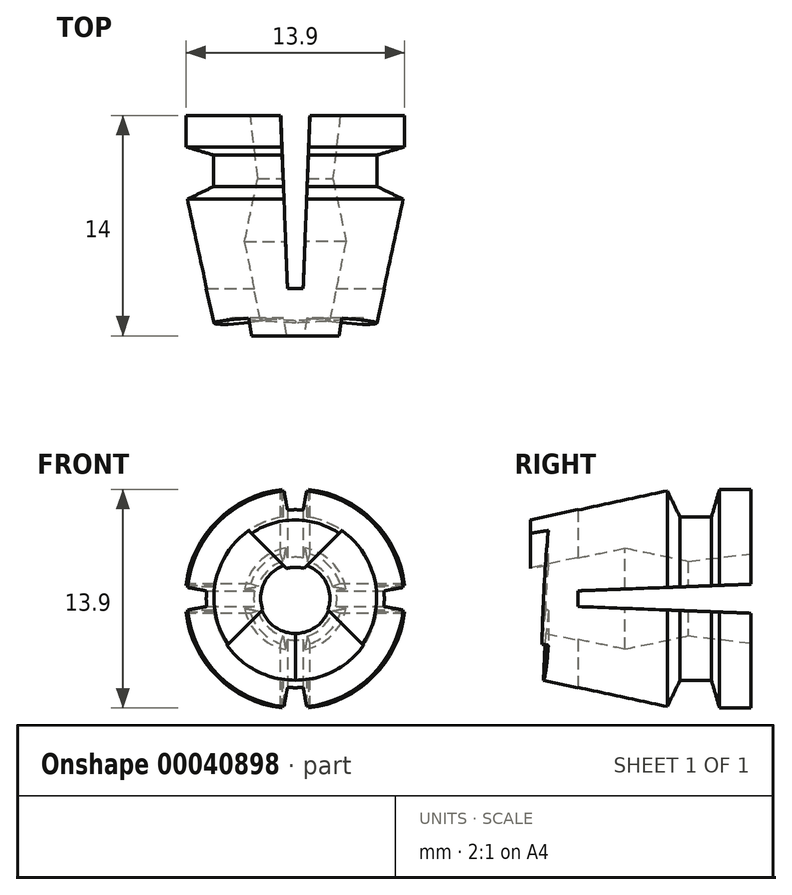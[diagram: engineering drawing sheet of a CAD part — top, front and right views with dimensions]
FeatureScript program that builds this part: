
annotation { "Feature Type Name" : "Feature", "Feature Type Description" : "" }
export const myFeature = defineFeature(function(context is Context, id is Id, definition is map)
    precondition{}
    {
        {
            var Q0;
            Q0=qCreatedBy(makeId("Top.planeOp"),FACE);
            var sketch = newSketch(context, id + "F0", { "sketchPlane" : qUnion([Q0])});
            skLineSegment(sketch, "E0", {"start": v(3, 14) * mm, "end": v(7, 14) * mm});
            skLineSegment(sketch, "E1", {"start": v(7, 14) * mm, "end": v(7, 12) * mm});
            skLineSegment(sketch, "E2", {"start": v(6.89, 8.67) * mm, "end": v(5, 0) * mm});
            skLineSegment(sketch, "E3", {"start": v(5, 0) * mm, "end": v(2, 0) * mm});
            skLineSegment(sketch, "E4", {"start": v(2, 0) * mm, "end": v(3.28, 6) * mm});
            skLineSegment(sketch, "E5", {"start": v(3.28, 6) * mm, "end": v(3.28, 6) * mm});
            skLineSegment(sketch, "E6", {"start": v(3.28, 6) * mm, "end": v(2.5, 10) * mm});
            skLineSegment(sketch, "E7", {"start": v(2.5, 10) * mm, "end": v(2.38, 10) * mm});
            skLineSegment(sketch, "E8", {"start": v(2.5, 10) * mm, "end": v(3, 14) * mm});
            skLineSegment(sketch, "E9", {"start": v(0, 20.25) * mm, "end": v(0, -12.85) * mm, "construction": true});
            skLineSegment(sketch, "E10", {"start": v(7, 12) * mm, "end": v(5.25, 11.48) * mm});
            skLineSegment(sketch, "E11", {"start": v(5.25, 11.48) * mm, "end": v(5.25, 9.48) * mm});
            skLineSegment(sketch, "E12", {"start": v(5.25, 9.48) * mm, "end": v(6.89, 8.67) * mm});
            skSolve(sketch);
        }
        {
            var Q0;
            Q0=makeQuery(id+"F0.imprint","IMPRINT",FACE,{"disambiguationData":[TD([[makeQuery(id+"F0.imprint","IMPRINT",EDGE,{"derivedFrom":sQuery(id+"F0.wireOp",EDGE,"E0")}),-1.0]])]});
            var Q1;
            Q1=sQuery(id+"F0.wireOp",EDGE,"E9");
            revolve(context, id + "F1", {"entities" : qUnion([Q0]), "axis" : qUnion([Q1]), "revolveType" : RevolveType.FULL});
        }
        {
            var Q0;
            Q0=qCreatedBy(makeId("Top.planeOp"),FACE);
            var sketch = newSketch(context, id + "F2", { "sketchPlane" : qUnion([Q0])});
            skLineSegment(sketch, "E13.rect.bottom", {"start": v(0.5, 3) * mm, "end": v(0, 3) * mm});
            skLineSegment(sketch, "E13.rect.top", {"start": v(1, 16) * mm, "end": v(0, 16) * mm});
            skLineSegment(sketch, "E13.rect.left", {"start": v(0.5, 3) * mm, "end": v(1, 16) * mm});
            skLineSegment(sketch, "E13.rect.right", {"start": v(-0.5, 3) * mm, "end": v(-1, 16) * mm});
            skPoint(sketch, "E13.rect.middle", {"position": v(0, 35.46) * mm});
            skLineSegment(sketch, "E14", {"start": v(0, 16) * mm, "end": v(-1, 16) * mm});
            skLineSegment(sketch, "E15", {"start": v(0, 3) * mm, "end": v(-0.5, 3) * mm});
            skSolve(sketch);
        }
        {
            var Q0;
            Q0 = qSketchRegion(id + "F2", true);
            extrude(context, id + "F3", {"entities" : qUnion([Q0]), "depth" : 25.4 * mm, "symmetric" : true});
        }
        {
            var Q0;
            Q0=makeQuery(id+"F3.opExtrude","SWEPT_BODY",BODY,{"disambiguationData":[OSD([sQuery(id+"F2.wireOp",EDGE,"E13.rect.bottom"),sQuery(id+"F2.wireOp",EDGE,"E13.rect.top"),sQuery(id+"F2.wireOp",EDGE,"E13.rect.left"),sQuery(id+"F2.wireOp",EDGE,"E13.rect.right")])]});
            var Q1;
            Q1=sQuery(id+"F0.wireOp",EDGE,"E9");
            circularPattern(context, id + "F4", {"entities" : qUnion([Q0]), "axis" : qUnion([Q1]), "angle" : 90 * degree, "instanceCount" : 2, "computeTransformsWithoutBuiltin" : true});
        }
        {
            var Q0;
            Q0=makeQuery(id+"F3.opExtrude","SWEPT_BODY",BODY,{"disambiguationData":[OSD([sQuery(id+"F2.wireOp",EDGE,"E13.rect.bottom"),sQuery(id+"F2.wireOp",EDGE,"E13.rect.top"),sQuery(id+"F2.wireOp",EDGE,"E13.rect.left"),sQuery(id+"F2.wireOp",EDGE,"E13.rect.right")])]});
            var Q1;
            Q1=makeQuery(id+"F4.opPattern","COPY",BODY,{"derivedFrom":makeQuery(id+"F3.opExtrude","SWEPT_BODY",BODY,{"disambiguationData":[OSD([sQuery(id+"F2.wireOp",EDGE,"E13.rect.bottom"),sQuery(id+"F2.wireOp",EDGE,"E13.rect.top"),sQuery(id+"F2.wireOp",EDGE,"E13.rect.left"),sQuery(id+"F2.wireOp",EDGE,"E13.rect.right")])]}),"instanceName":"1"});
            var Q2;
            Q2=makeQuery(id+"F1.opRevolve","SWEPT_BODY",BODY,{"disambiguationData":[OSD([sQuery(id+"F0.wireOp",EDGE,"E0"),sQuery(id+"F0.wireOp",EDGE,"E1"),sQuery(id+"F0.wireOp",EDGE,"36a073ee-a093-49fd-890a-3c94928a5ffd"),sQuery(id+"F0.wireOp",EDGE,"E2"),sQuery(id+"F0.wireOp",EDGE,"E3"),sQuery(id+"F0.wireOp",EDGE,"E4"),sQuery(id+"F0.wireOp",EDGE,"E5"),sQuery(id+"F0.wireOp",EDGE,"E6"),sQuery(id+"F0.wireOp",EDGE,"E7"),sQuery(id+"F0.wireOp",EDGE,"E8")])]});
            booleanBodies(context, id + "F5", {"operationType" : BooleanOperationType.SUBTRACTION, "tools" : qUnion([Q0, Q1]), "targets" : qUnion([Q2])});
        }
        {
            var Q0;
            Q0=sQuery(id+"F0.wireOp",EDGE,"E9");
            cPlane(context, id + "F6", {"entities" : qUnion([Q0]), "cplaneType" : CPlaneType.LINE_ANGLE, "offset" : 152.4 * mm, "angle" : 45 * degree, "width" : 152.4 * mm, "height" : 152.4 * mm});
        }
        {
            var Q0;
            Q0=qCreatedBy(id+"F6.planeOp",FACE);
            var sketch = newSketch(context, id + "F7", { "sketchPlane" : qUnion([Q0])});
            skLineSegment(sketch, "E16.rect.bottom", {"start": v(1.13, 0.98) * mm, "end": v(-1.13, 0.98) * mm});
            skLineSegment(sketch, "E16.rect.top", {"start": v(0.38, -10.02) * mm, "end": v(-0.38, -10.02) * mm});
            skLineSegment(sketch, "E16.rect.left", {"start": v(1.13, 0.98) * mm, "end": v(0.38, -10.02) * mm});
            skLineSegment(sketch, "E16.rect.right", {"start": v(-1.13, 0.98) * mm, "end": v(-0.38, -10.02) * mm});
            skPoint(sketch, "E16.rect.middle", {"position": v(0, -4.52) * mm});
            skPoint(sketch, "E17", {"position": v(0, 0.98) * mm});
            skPoint(sketch, "E18", {"position": v(0, -10.02) * mm});
            skSolve(sketch);
        }
        {
            var Q0;
            Q0 = qSketchRegion(id + "F7", true);
            extrude(context, id + "F8", {"entities" : qUnion([Q0]), "depth" : 25.4 * mm, "symmetric" : true});
        }
        {
            var Q0;
            Q0=makeQuery(id+"F8.opExtrude","SWEPT_BODY",BODY,{"disambiguationData":[OSD([sQuery(id+"F7.wireOp",EDGE,"E16.rect.bottom"),sQuery(id+"F7.wireOp",EDGE,"E16.rect.top"),sQuery(id+"F7.wireOp",EDGE,"E16.rect.left"),sQuery(id+"F7.wireOp",EDGE,"E16.rect.right")])]});
            var Q1;
            Q1=sQuery(id+"F0.wireOp",EDGE,"E9");
            circularPattern(context, id + "F9", {"entities" : qUnion([Q0]), "axis" : qUnion([Q1]), "angle" : 90 * degree, "instanceCount" : 2, "computeTransformsWithoutBuiltin" : true});
        }
        {
            var Q0;
            Q0=makeQuery(id+"F8.opExtrude","SWEPT_BODY",BODY,{"disambiguationData":[OSD([sQuery(id+"F7.wireOp",EDGE,"E16.rect.bottom"),sQuery(id+"F7.wireOp",EDGE,"E16.rect.top"),sQuery(id+"F7.wireOp",EDGE,"E16.rect.left"),sQuery(id+"F7.wireOp",EDGE,"E16.rect.right")])]});
            var Q1;
            Q1=makeQuery(id+"F9.opPattern","COPY",BODY,{"derivedFrom":makeQuery(id+"F8.opExtrude","SWEPT_BODY",BODY,{"disambiguationData":[OSD([sQuery(id+"F7.wireOp",EDGE,"E16.rect.bottom"),sQuery(id+"F7.wireOp",EDGE,"E16.rect.top"),sQuery(id+"F7.wireOp",EDGE,"E16.rect.left"),sQuery(id+"F7.wireOp",EDGE,"E16.rect.right")])]}),"instanceName":"1"});
            var Q2;
            Q2=makeQuery(id+"F1.opRevolve","SWEPT_BODY",BODY,{"disambiguationData":[OSD([sQuery(id+"F0.wireOp",EDGE,"E0"),sQuery(id+"F0.wireOp",EDGE,"E1"),sQuery(id+"F0.wireOp",EDGE,"36a073ee-a093-49fd-890a-3c94928a5ffd"),sQuery(id+"F0.wireOp",EDGE,"E2"),sQuery(id+"F0.wireOp",EDGE,"E3"),sQuery(id+"F0.wireOp",EDGE,"E4"),sQuery(id+"F0.wireOp",EDGE,"E5"),sQuery(id+"F0.wireOp",EDGE,"E6"),sQuery(id+"F0.wireOp",EDGE,"E7"),sQuery(id+"F0.wireOp",EDGE,"E8")])]});
            booleanBodies(context, id + "F10", {"operationType" : BooleanOperationType.SUBTRACTION, "tools" : qUnion([Q0, Q1]), "targets" : qUnion([Q2])});
        }
    });
